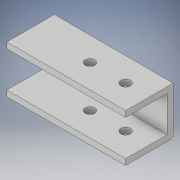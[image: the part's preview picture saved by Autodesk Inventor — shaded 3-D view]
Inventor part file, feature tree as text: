
AUTODESK INVENTOR PART (.ipt)
format: ipt  version: 2018 (Build 220112000, 112)  size: 116,224 bytes
history: native  units: in
note: dims shown in document units (in); Inventor stores cm internally (conversion verified against a paired STEP export)
features: sketch x4, other x3
ambient origin geometry x8: Origin, YZ Plane, XZ Plane, XY Plane, X Axis, Y Axis, Z Axis, Center Point
bodies: Solid1 (feature_tree)
feature tree (7):
  other  "wheel tip connector 1.ipt"
  other  "Solid1::wheel tip connector 1.ipt"
  other  "TaggingFeature1"
  sketch  "Sketch1"  dims[d0=0.3937in]
  sketch  "Sketch2"
  sketch  "Sketch3"
  sketch  "Sketch4"
